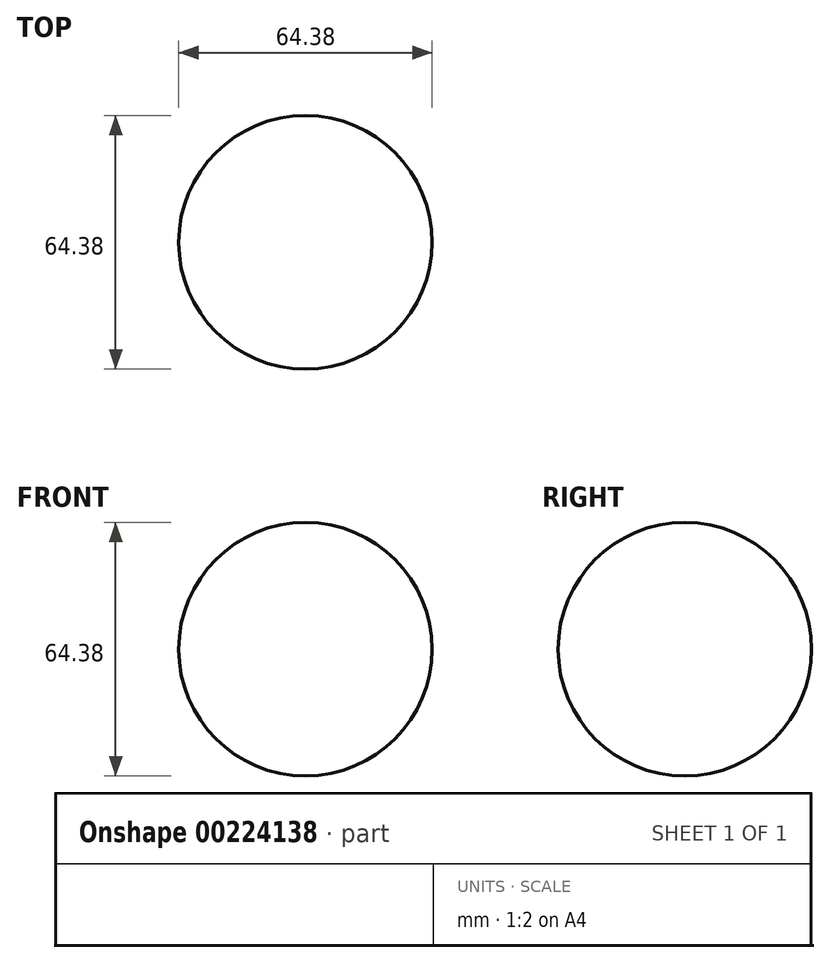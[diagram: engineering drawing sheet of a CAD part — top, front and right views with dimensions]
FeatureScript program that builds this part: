
annotation { "Feature Type Name" : "Feature", "Feature Type Description" : "" }
export const myFeature = defineFeature(function(context is Context, id is Id, definition is map)
    precondition{}
    {
        {
            var Q0;
            Q0=qCreatedBy(makeId("Front.planeOp"),FACE);
            var sketch = newSketch(context, id + "F0", { "sketchPlane" : qUnion([Q0])});
            skCircle(sketch, "E0", {"center": v(0, 0) * mm, "radius": 32.19 * mm});
            skLineSegment(sketch, "E1", {"start": v(0, 32.19) * mm, "end": v(0, -32.19) * mm});
            skSolve(sketch);
        }
        {
            var Q0;
            {var subQ0=sQuery(id+"F0.wireOp",EDGE,"E1");Q0=makeQuery(id+"F0.imprint","IMPRINT",FACE,{"disambiguationData":[TD([[makeQuery(id+"F0.imprint","IMPRINT",EDGE,{"derivedFrom":subQ0}),1.0]])]});}
            var Q1;
            Q1=sQuery(id+"F0.wireOp",EDGE,"E1");
            revolve(context, id + "F1", {"entities" : qUnion([Q0]), "axis" : qUnion([Q1]), "revolveType" : RevolveType.FULL});
        }
    });
